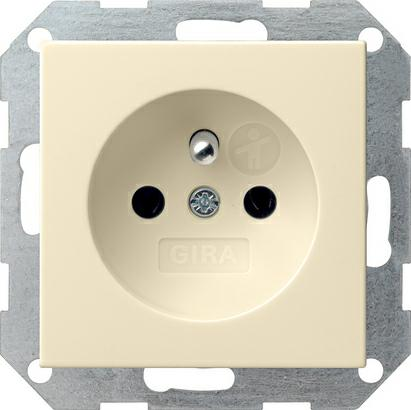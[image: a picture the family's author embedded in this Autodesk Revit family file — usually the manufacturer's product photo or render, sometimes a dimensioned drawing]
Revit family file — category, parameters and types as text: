
# Revit family: E_Cable Junction Box_F_MEPcontent_Spelsberg_IBTronic XL_INT-EN
name_source: partatom
category: Electrical Fixtures
revit_build: Autodesk Revit 2017 (Build: 20160225_1515(x64)
units: mm (PartAtom-declared; Revit-internal decimal feet)

## family parameters
Cut with Voids When Loaded = No
Host = Face
Maintain Annotation Orientation = Yes
OmniClass Number = 23.80.30.14.24
OmniClass Title = Junction Boxes
Part Type = Junction Box
Room Calculation Point = No
Round Connector Dimension = Use Diameter
Shared = No

## types (2) — shared parameters
3D Representation = 3DGeometry
ETIM Article Class = EC000414
Height = 92 mm  [stored 0.301837 ft]
IFCExportAs = IfcJunctionBox
IFCExportType = NOTDEFINED
Length = 280 mm  [stored 0.918635 ft]
Manufacturer = Spelsberg
Manufacturer URL = http://www.spelsberg.com
Product Line = Spelsberg
Revit Version = 2017
Rotation U-Axis Correction = 0.00°
Rotation U-Axis Default Correction = 0.00°
Rotation V-Axis Correction = 0.00°
Rotation V-Axis Default Correction = 0.00°
Rotation W-Axis Correction = 0.00°
Rotation W-Axis Default Correction = 0.00°
Voltage = 230 V
Width = 252 mm  [stored 0.826772 ft]
zero-valued in all types: Default Elevation

## per-type parameters (varying)
| type | Article Description | Bottom Offset | Conduit Diameter 1 | Conduit Diameter 2 | Description | Manufacturer Art. No. | Side Distance | Side Offset |
| IBTronic XL H 185 F | Enclosure IBTronic XL H 185 F | 62 mm | 20 mm  [stored 0.0656168 ft] | 25 mm  [stored 0.082021 ft] | Enclosure IBTronic XL H 185 F | 97660401 | 25 mm  [stored 0.082021 ft] | 2 mm  [stored 0.00656168 ft] |
| IBTronic XL H 185 FE | Enclosure IBTronic XL H 185 FE | 63 mm | 16 mm  [stored 0.0524934 ft] | 19 mm  [stored 0.062336 ft] | Enclosure IBTronic XL H 185 FE | 97660402 | 24 mm  [stored 0.0787402 ft] | 7 mm  [stored 0.0229659 ft] |

note: column(s) folded — value = type name in every type: Article Type, Model

note: [stored X ft] marks values corroborated as IEEE doubles in the binary element streams (Revit-internal decimal feet)

## geometry (parser evidence)
native form markers: Sweep x21
no freeform markers — native parametric forms only
